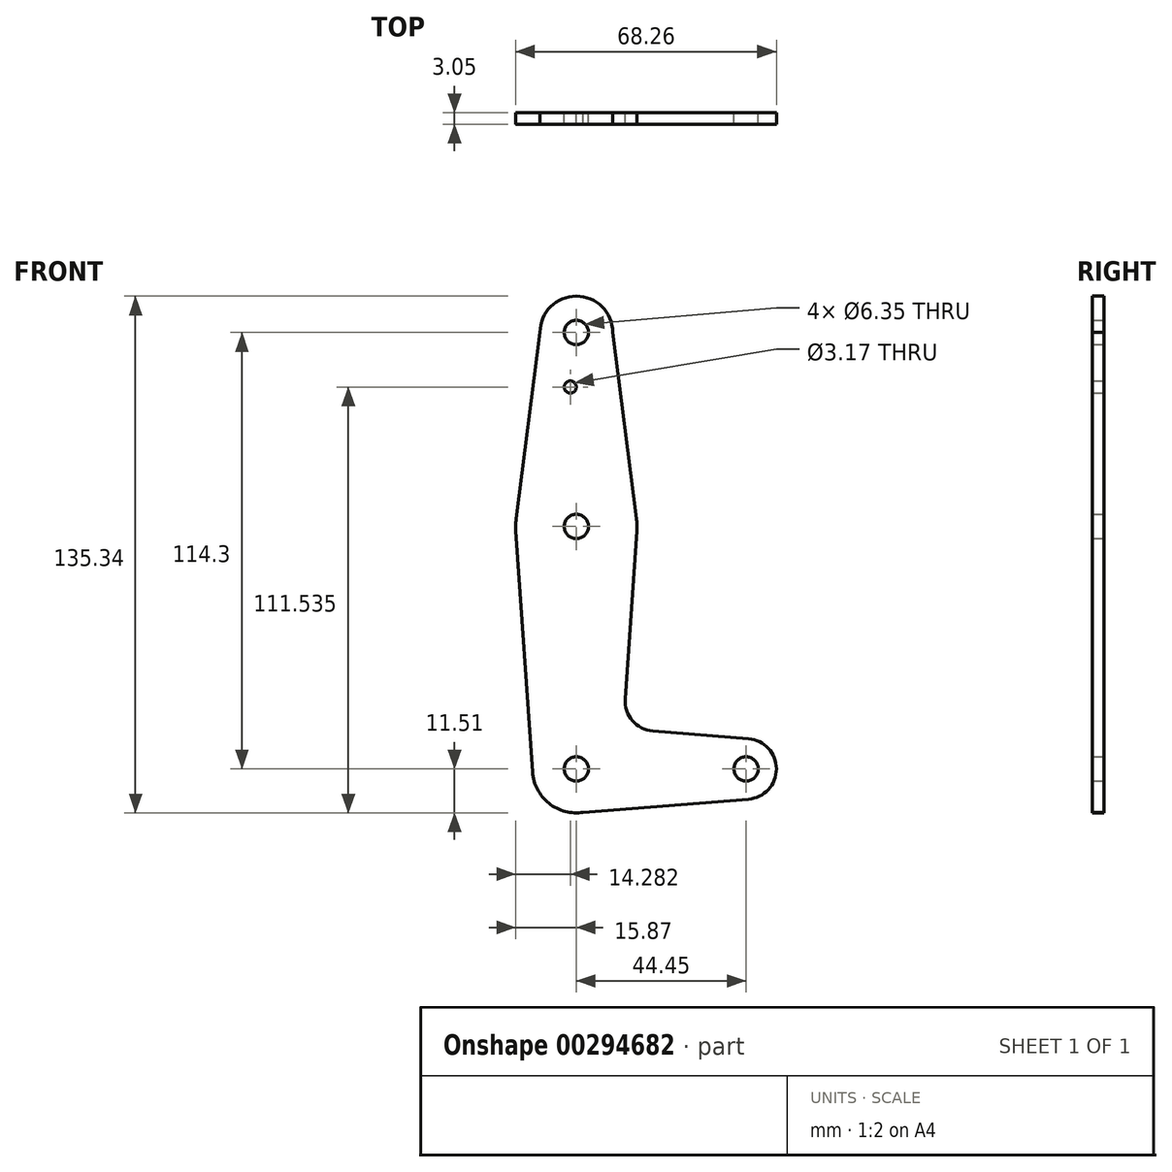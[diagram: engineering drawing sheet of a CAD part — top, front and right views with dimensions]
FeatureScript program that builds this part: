
annotation { "Feature Type Name" : "Feature", "Feature Type Description" : "" }
export const myFeature = defineFeature(function(context is Context, id is Id, definition is map)
    precondition{}
    {
        {
            var Q0;
            Q0=qCreatedBy(makeId("Front.planeOp"),FACE);
            var sketch = newSketch(context, id + "F0", { "sketchPlane" : qUnion([Q0])});
            skCircle(sketch, "E0", {"center": v(0, 0) * mm, "radius": 11.5 * mm});
            skCircle(sketch, "E1", {"center": v(44.45, 0) * mm, "radius": 7.94 * mm});
            skCircle(sketch, "E2", {"center": v(0, 63.5) * mm, "radius": 15.88 * mm});
            skCircle(sketch, "E3", {"center": v(0, 114.3) * mm, "radius": 9.53 * mm});
            skLineSegment(sketch, "E4", {"start": v(0, 114.3) * mm, "end": v(0, 63.5) * mm, "construction": true});
            skLineSegment(sketch, "E5", {"start": v(0, 63.5) * mm, "end": v(0, 0) * mm, "construction": true});
            skLineSegment(sketch, "E6", {"start": v(0, 0) * mm, "end": v(44.45, 0) * mm, "construction": true});
            skLineSegment(sketch, "E7", {"start": v(9.52, 114.36) * mm, "end": v(15.75, 65.5) * mm});
            skLineSegment(sketch, "E8", {"start": v(-9.52, 114.39) * mm, "end": v(-15.75, 65.5) * mm});
            skLineSegment(sketch, "E9", {"start": v(20.1, 9.9) * mm, "end": v(45.08, 7.91) * mm});
            skLineSegment(sketch, "E10", {"start": v(0, -11.5) * mm, "end": v(45.08, -7.91) * mm});
            skLineSegment(sketch, "E11", {"start": v(15.84, 62.4) * mm, "end": v(12.8, 18.38) * mm});
            skLineSegment(sketch, "E12", {"start": v(-15.84, 62.4) * mm, "end": v(-11.48, -0.8) * mm});
            skCircle(sketch, "E13", {"center": v(0, 114.3) * mm, "radius": 3.18 * mm});
            skCircle(sketch, "E14", {"center": v(-1.59, 100.03) * mm, "radius": 1.59 * mm});
            skCircle(sketch, "E15", {"center": v(0, 0) * mm, "radius": 3.18 * mm});
            skCircle(sketch, "E16", {"center": v(44.45, 0) * mm, "radius": 3.18 * mm});
            skArc(sketch, "E17.filletArc", {"start": v(12.8, 18.38) * mm, "mid": v(14.7, 12.64) * mm, "end": v(20.1, 9.9) * mm});
            skCircle(sketch, "E18", {"center": v(0, 63.5) * mm, "radius": 3.18 * mm});
            skSolve(sketch);
        }
        {
            var Q0;
            Q0 = qSketchRegion(id + "F0", true);
            extrude(context, id + "F1", {"entities" : qUnion([Q0]), "depth" : 3.05 * mm});
        }
    });
